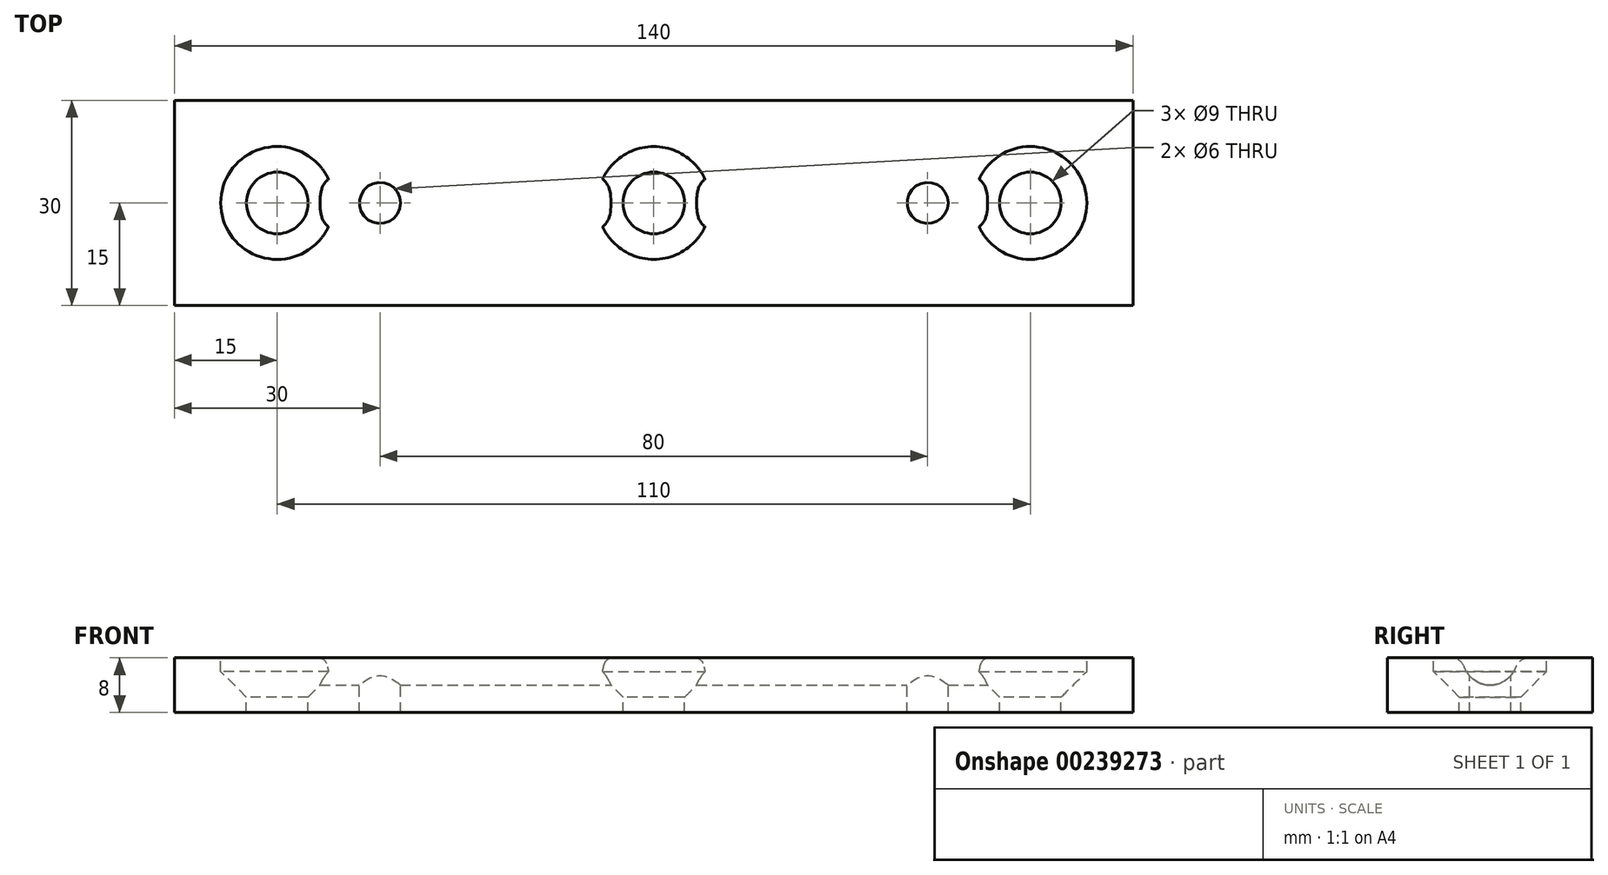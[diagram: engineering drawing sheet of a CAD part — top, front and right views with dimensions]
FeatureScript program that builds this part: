
annotation { "Feature Type Name" : "Feature", "Feature Type Description" : "" }
export const myFeature = defineFeature(function(context is Context, id is Id, definition is map)
    precondition{}
    {
        {
            var Q0;
            Q0=qCreatedBy(makeId("Top.planeOp"),FACE);
            var sketch = newSketch(context, id + "F0", { "sketchPlane" : qUnion([Q0])});
            skLineSegment(sketch, "E0.bottom", {"start": v(-70, 15) * mm, "end": v(70, 15) * mm});
            skLineSegment(sketch, "E0.top", {"start": v(-70, -15) * mm, "end": v(70, -15) * mm});
            skLineSegment(sketch, "E0.left", {"start": v(-70, 15) * mm, "end": v(-70, -15) * mm});
            skLineSegment(sketch, "E0.right", {"start": v(70, 15) * mm, "end": v(70, -15) * mm});
            skPoint(sketch, "E0.middle", {"position": v(0, 0) * mm});
            skSolve(sketch);
        }
        {
            var Q0;
            Q0 = qSketchRegion(id + "F0", true);
            extrude(context, id + "F1", {"entities" : qUnion([Q0]), "depth" : 8 * mm});
        }
        {
            var Q0;
            Q0=makeQuery(id+"F1.opExtrude","CAP_FACE",FACE,{"disambiguationData":[OSD([sQuery(id+"F0.wireOp",EDGE,"E0.bottom"),sQuery(id+"F0.wireOp",EDGE,"E0.top"),sQuery(id+"F0.wireOp",EDGE,"E0.left"),sQuery(id+"F0.wireOp",EDGE,"E0.right")])],"isStart":false});
            var sketch = newSketch(context, id + "F2", { "sketchPlane" : qUnion([Q0])});
            skLineSegment(sketch, "E1", {"start": v(-92.77, 0) * mm, "end": v(91.66, 0) * mm, "construction": true});
            skLineSegment(sketch, "E2", {"start": v(0, 45.33) * mm, "end": v(0, -31.87) * mm, "construction": true});
            skPoint(sketch, "E2.endSnap0", {"position": v(0, -15) * mm});
            skLineSegment(sketch, "E3.0", {"start": v(-55, 45.33) * mm, "end": v(-55, -31.87) * mm, "construction": true});
            skCircle(sketch, "E4", {"center": v(-55, 0) * mm, "radius": 8.25 * mm});
            skCircle(sketch, "E5.1.0.0", {"center": v(0, 0) * mm, "radius": 8.25 * mm});
            skCircle(sketch, "E5.2.0.0", {"center": v(55, 0) * mm, "radius": 8.25 * mm});
            skLineSegment(sketch, "E5.direction1", {"start": v(-55, 0) * mm, "end": v(0, 0) * mm, "construction": true});
            skSolve(sketch);
        }
        {
            var Q0;
            Q0 = qSketchRegion(id + "F2", true);
            extrude(context, id + "F3", {"entities" : qUnion([Q0]), "operationType" : NewBodyOperationType.REMOVE, "oppositeDirection" : true, "depth" : 2 * mm});
        }
        {
            var Q0;
            Q0=makeQuery(id+"F3.boolean.opBoolean","COPY",FACE,{"derivedFrom":makeQuery(id+"F3.opExtrude","CAP_FACE",FACE,{"disambiguationData":[OSD([sQuery(id+"F2.wireOp",EDGE,"E4")])],"isStart":false})});
            var sketch = newSketch(context, id + "F4", { "sketchPlane" : qUnion([Q0])});
            skCircle(sketch, "E6.0", {"center": v(-55, 0) * mm, "radius": 8.25 * mm, "construction": true});
            skPoint(sketch, "E7.1.0.0", {"position": v(0, 0) * mm});
            skPoint(sketch, "E7.2.0.0", {"position": v(55, 0) * mm});
            skLineSegment(sketch, "E7.direction1", {"start": v(-55, 0) * mm, "end": v(0, 0) * mm, "construction": true});
            skSolve(sketch);
        }
        {
            var Q0;
            Q0=sQuery(id+"F4.wireOp",VERTEX,"E6.0.center");
            var Q1;
            Q1=sQuery(id+"F4.wireOp",VERTEX,"E7.1.0.0");
            var Q2;
            Q2=sQuery(id+"F4.wireOp",VERTEX,"E7.2.0.0");
            var Q3;
            Q3=makeQuery(id+"F1.opExtrude","SWEPT_BODY",BODY,{"disambiguationData":[OSD([sQuery(id+"F0.wireOp",EDGE,"E0.bottom"),sQuery(id+"F0.wireOp",EDGE,"E0.top"),sQuery(id+"F0.wireOp",EDGE,"E0.left"),sQuery(id+"F0.wireOp",EDGE,"E0.right")])]});
            hole(context, id + "F5", {"style" : HoleStyle.C_SINK, "endStyle" : HoleEndStyle.THROUGH, "standardTappedOrClearance" : lookupTablePath({ "standard" : "ISO", "size" : "9", "type" : "Drilled" }), "standardBlindInLast" : lookupTablePath({ "standard" : "ISO", "size" : "9", "type" : "Drilled" }), "holeDiameter" : 9 * mm, "cSinkDiameter" : 16.5 * mm, "cSinkAngle" : 90 * degree, "locations" : qUnion([Q0, Q1, Q2]), "scope" : qUnion([Q3]), "isTappedThrough" : true});
        }
        {
            var Q0;
            Q0=qCreatedBy(makeId("Right.planeOp"),FACE);
            var sketch = newSketch(context, id + "F6", { "sketchPlane" : qUnion([Q0])});
            skLineSegment(sketch, "E8.0.0", {"start": v(15, 8) * mm, "end": v(-15, 8) * mm, "construction": true});
            skLineSegment(sketch, "E8.0.2", {"start": v(-15, 8) * mm, "end": v(15, 8) * mm, "construction": true});
            skCircle(sketch, "E9", {"center": v(0, 8) * mm, "radius": 4 * mm});
            skSolve(sketch);
        }
        {
            var Q0;
            Q0 = qSketchRegion(id + "F6", true);
            extrude(context, id + "F7", {"entities" : qUnion([Q0]), "operationType" : NewBodyOperationType.REMOVE, "endBound" : BoundingType.SYMMETRIC, "oppositeDirection" : true, "depth" : 110 * mm});
        }
        {
            var Q0;
            Q0=makeQuery(id+"F7.boolean.opBoolean","INTERSECT",EDGE,{"disambiguationData":[OD(1.0)],"derivedFrom":[makeQuery(id+"F1.opExtrude","CAP_FACE",FACE,{"disambiguationData":[OSD([sQuery(id+"F0.wireOp",EDGE,"E0.bottom"),sQuery(id+"F0.wireOp",EDGE,"E0.top"),sQuery(id+"F0.wireOp",EDGE,"E0.left"),sQuery(id+"F0.wireOp",EDGE,"E0.right")])],"isStart":false}),makeQuery(id+"F7.opExtrude","SWEPT_FACE",FACE,{"disambiguationData":[OSD([sQuery(id+"F6.wireOp",EDGE,"E9")])]})]});
            var Q1;
            Q1=makeQuery(id+"F7.boolean.opBoolean","INTERSECT",EDGE,{"disambiguationData":[OD(3.0)],"derivedFrom":[makeQuery(id+"F1.opExtrude","CAP_FACE",FACE,{"disambiguationData":[OSD([sQuery(id+"F0.wireOp",EDGE,"E0.bottom"),sQuery(id+"F0.wireOp",EDGE,"E0.top"),sQuery(id+"F0.wireOp",EDGE,"E0.left"),sQuery(id+"F0.wireOp",EDGE,"E0.right")])],"isStart":false}),makeQuery(id+"F7.opExtrude","SWEPT_FACE",FACE,{"disambiguationData":[OSD([sQuery(id+"F6.wireOp",EDGE,"E9")])]})]});
            var Q2;
            Q2=makeQuery(id+"F7.boolean.opBoolean","INTERSECT",EDGE,{"disambiguationData":[OD(0.0)],"derivedFrom":[makeQuery(id+"F1.opExtrude","CAP_FACE",FACE,{"disambiguationData":[OSD([sQuery(id+"F0.wireOp",EDGE,"E0.bottom"),sQuery(id+"F0.wireOp",EDGE,"E0.top"),sQuery(id+"F0.wireOp",EDGE,"E0.left"),sQuery(id+"F0.wireOp",EDGE,"E0.right")])],"isStart":false}),makeQuery(id+"F7.opExtrude","SWEPT_FACE",FACE,{"disambiguationData":[OSD([sQuery(id+"F6.wireOp",EDGE,"E9")])]})]});
            var Q3;
            Q3=makeQuery(id+"F7.boolean.opBoolean","INTERSECT",EDGE,{"disambiguationData":[OD(2.0)],"derivedFrom":[makeQuery(id+"F1.opExtrude","CAP_FACE",FACE,{"disambiguationData":[OSD([sQuery(id+"F0.wireOp",EDGE,"E0.bottom"),sQuery(id+"F0.wireOp",EDGE,"E0.top"),sQuery(id+"F0.wireOp",EDGE,"E0.left"),sQuery(id+"F0.wireOp",EDGE,"E0.right")])],"isStart":false}),makeQuery(id+"F7.opExtrude","SWEPT_FACE",FACE,{"disambiguationData":[OSD([sQuery(id+"F6.wireOp",EDGE,"E9")])]})]});
            fillet(context, id + "F8", {"entities" : qUnion([Q0, Q1, Q2, Q3]), "radius" : 2 * mm, "tangentPropagation" : true, "allowEdgeOverflow" : false});
        }
        {
            var Q0;
            Q0=makeQuery(id+"F1.opExtrude","CAP_FACE",FACE,{"disambiguationData":[OSD([sQuery(id+"F0.wireOp",EDGE,"E0.bottom"),sQuery(id+"F0.wireOp",EDGE,"E0.top"),sQuery(id+"F0.wireOp",EDGE,"E0.left"),sQuery(id+"F0.wireOp",EDGE,"E0.right")])],"isStart":false});
            var sketch = newSketch(context, id + "F9", { "sketchPlane" : qUnion([Q0])});
            skLineSegment(sketch, "E10", {"start": v(0, 35.15) * mm, "end": v(0, -22.87) * mm, "construction": true});
            skLineSegment(sketch, "E11", {"start": v(-80.6, 0) * mm, "end": v(81.16, 0) * mm, "construction": true});
            skPoint(sketch, "E11.startSnap0", {"position": v(-63.25, 0) * mm});
            skLineSegment(sketch, "E12.0", {"start": v(-40, 35.15) * mm, "end": v(-40, -22.87) * mm, "construction": true});
            skPoint(sketch, "E13", {"position": v(-40, 0) * mm});
            skPoint(sketch, "E14.MirrorP", {"position": v(40, 0) * mm});
            skSolve(sketch);
        }
        {
            var Q0;
            Q0=sQuery(id+"F9.wireOp",VERTEX,"E13");
            var Q1;
            Q1=sQuery(id+"F9.wireOp",VERTEX,"E14.MirrorP");
            var Q2;
            Q2=makeQuery(id+"F1.opExtrude","SWEPT_BODY",BODY,{"disambiguationData":[OSD([sQuery(id+"F0.wireOp",EDGE,"E0.bottom"),sQuery(id+"F0.wireOp",EDGE,"E0.top"),sQuery(id+"F0.wireOp",EDGE,"E0.left"),sQuery(id+"F0.wireOp",EDGE,"E0.right")])]});
            hole(context, id + "F10", {"style" : HoleStyle.SIMPLE, "endStyle" : HoleEndStyle.THROUGH, "standardTappedOrClearance" : lookupTablePath({ "standard" : "ISO", "size" : "6", "type" : "Drilled" }), "standardBlindInLast" : lookupTablePath({ "standard" : "ISO", "size" : "6", "type" : "Drilled" }), "holeDiameter" : 6 * mm, "locations" : qUnion([Q0, Q1]), "scope" : qUnion([Q2]), "isTappedThrough" : true});
        }
    });
